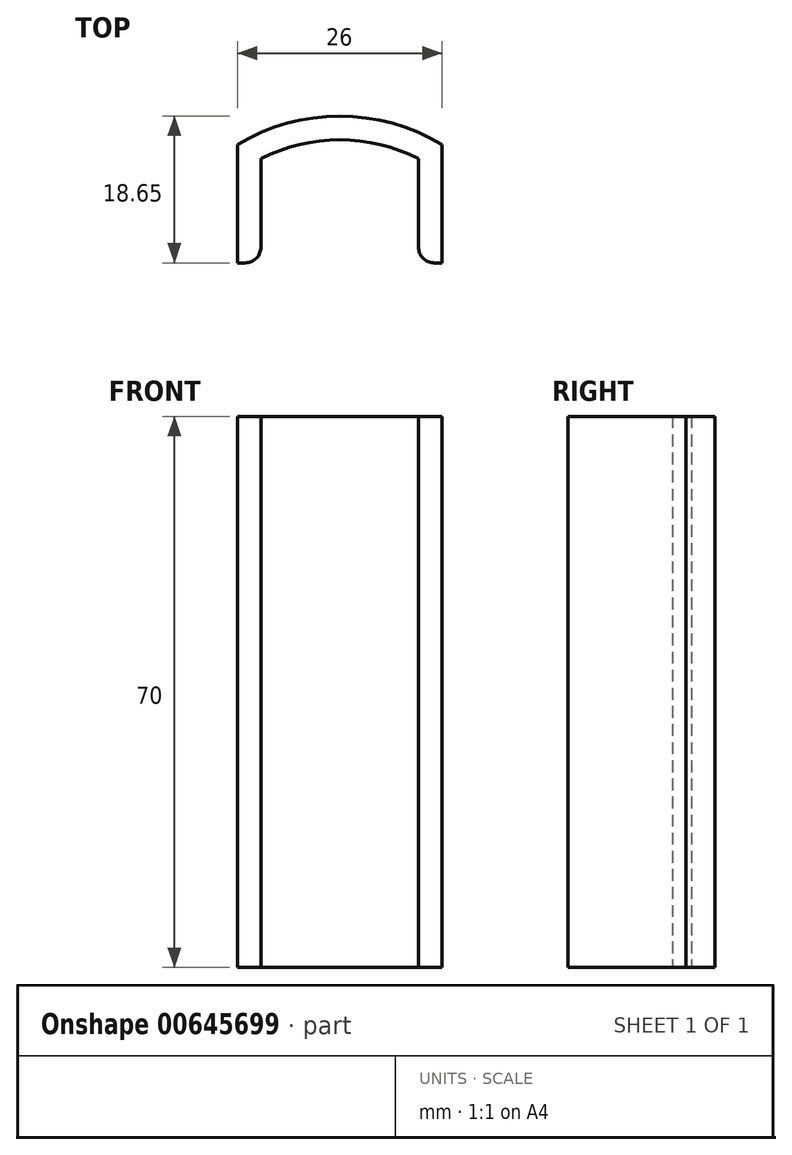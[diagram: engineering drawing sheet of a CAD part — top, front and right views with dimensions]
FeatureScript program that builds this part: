
annotation { "Feature Type Name" : "Feature", "Feature Type Description" : "" }
export const myFeature = defineFeature(function(context is Context, id is Id, definition is map)
    precondition{}
    {
        {
            var Q0;
            Q0=qCreatedBy(makeId("Top.planeOp"),FACE);
            var sketch = newSketch(context, id + "F0", { "sketchPlane" : qUnion([Q0])});
            skLineSegment(sketch, "E0", {"start": v(0, -55.13) * mm, "end": v(0, 49.41) * mm, "construction": true});
            skLineSegment(sketch, "E1.0", {"start": v(13, 0) * mm, "end": v(13, 15) * mm, "construction": true});
            skLineSegment(sketch, "E2", {"start": v(-42.47, 0) * mm, "end": v(41.45, 0) * mm, "construction": true});
            skArc(sketch, "E3", {"start": v(13, 15) * mm, "mid": v(0, 18.65) * mm, "end": v(-13, 15) * mm});
            skPoint(sketch, "E3.first.point", {"position": v(-13, 15) * mm});
            skPoint(sketch, "E3.second.point", {"position": v(13, 15) * mm});
            skPoint(sketch, "E3.third.point", {"position": v(0, -31.35) * mm});
            skArc(sketch, "E4.0", {"start": v(10, 13.24) * mm, "mid": v(0, 15.65) * mm, "end": v(-10, 13.24) * mm});
            skLineSegment(sketch, "E5.trimOffspring", {"start": v(-10, 0) * mm, "end": v(-10, 13.24) * mm, "construction": true});
            skLineSegment(sketch, "E6.trimOffspring", {"start": v(-13, 0) * mm, "end": v(-13, 15) * mm});
            skLineSegment(sketch, "E7.MirrorCS", {"start": v(-13, 0) * mm, "end": v(-13, 15) * mm, "construction": true});
            skLineSegment(sketch, "E8.MirrorCS", {"start": v(10, 0) * mm, "end": v(10, 13.24) * mm, "construction": true});
            skLineSegment(sketch, "E9", {"start": v(-13, 0) * mm, "end": v(-10, 0) * mm});
            skLineSegment(sketch, "E10", {"start": v(-10, 13.24) * mm, "end": v(-10, 0) * mm});
            skLineSegment(sketch, "E11", {"start": v(10, 13.24) * mm, "end": v(10, 0) * mm});
            skLineSegment(sketch, "E12", {"start": v(13, 15) * mm, "end": v(13, 0) * mm});
            skLineSegment(sketch, "E13", {"start": v(13, 0) * mm, "end": v(10, 0) * mm});
            skSolve(sketch);
        }
        {
            var Q0;
            Q0=makeQuery(id+"F0.imprint","IMPRINT",FACE,{"disambiguationData":[TD([[makeQuery(id+"F0.imprint","IMPRINT",EDGE,{"derivedFrom":sQuery(id+"F0.wireOp",EDGE,"E3")}),1.0]])]});
            extrude(context, id + "F1", {"entities" : qUnion([Q0]), "depth" : 70 * mm, "offsetDistance" : 25 * mm});
        }
        {
            var Q0;
            Q0=makeQuery(id+"F1.opExtrude","SWEPT_EDGE",EDGE,{"disambiguationData":[OSD([sQuery(id+"F0.wireOp",EDGE,"E9"),sQuery(id+"F0.wireOp",EDGE,"E10")])]});
            var Q1;
            Q1=makeQuery(id+"F1.opExtrude","SWEPT_EDGE",EDGE,{"disambiguationData":[OSD([sQuery(id+"F0.wireOp",EDGE,"E11"),sQuery(id+"F0.wireOp",EDGE,"E13")])]});
            fillet(context, id + "F2", {"entities" : qUnion([Q0, Q1]), "radius" : 2 * mm, "tangentPropagation" : true, "allowEdgeOverflow" : false});
        }
    });
